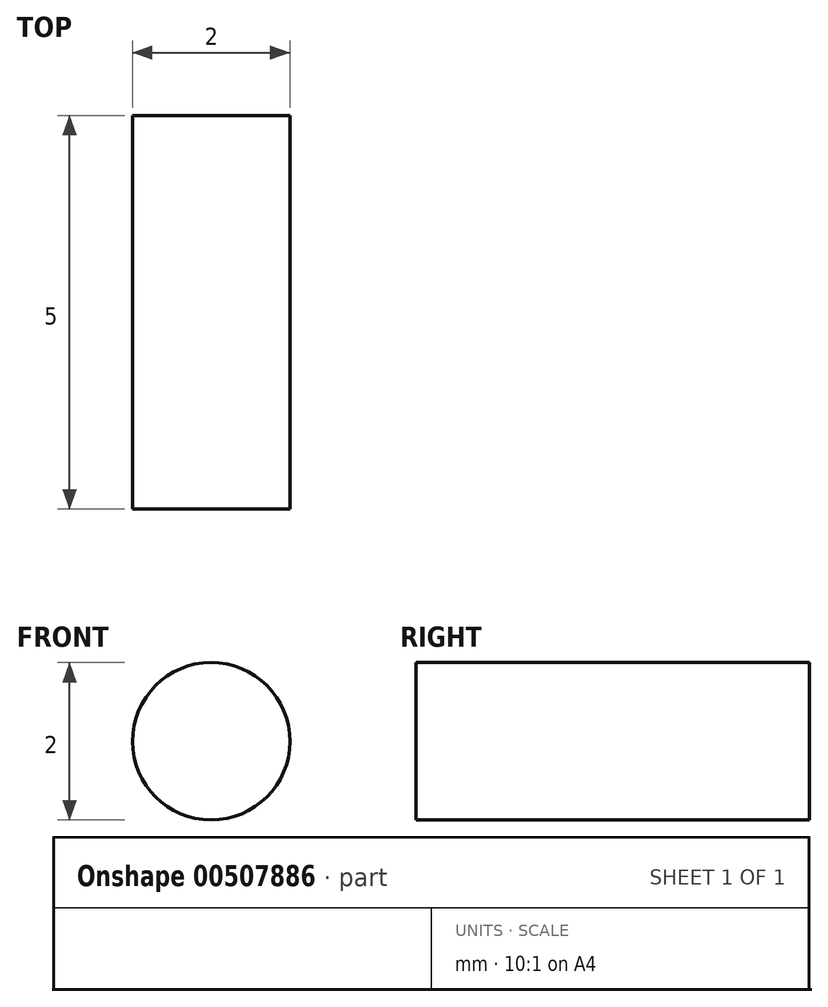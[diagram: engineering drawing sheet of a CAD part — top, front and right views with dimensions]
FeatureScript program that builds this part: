
annotation { "Feature Type Name" : "Feature", "Feature Type Description" : "" }
export const myFeature = defineFeature(function(context is Context, id is Id, definition is map)
    precondition{}
    {
        {
            var Q0;
            Q0=qCreatedBy(makeId("Front.planeOp"),FACE);
            var sketch = newSketch(context, id + "F0", { "sketchPlane" : qUnion([Q0])});
            skCircle(sketch, "E0", {"center": v(0, 0) * mm, "radius": 1 * mm});
            skSolve(sketch);
        }
        {
            var Q0;
            Q0=makeQuery(id+"F0.imprint","IMPRINT",FACE,{"disambiguationData":[TD([[makeQuery(id+"F0.imprint","IMPRINT",EDGE,{"derivedFrom":sQuery(id+"F0.wireOp",EDGE,"E0")}),1.0]])]});
            extrude(context, id + "F1", {"entities" : qUnion([Q0]), "depth" : 5 * mm, "offsetDistance" : 25 * mm, "symmetric" : true});
        }
    });
